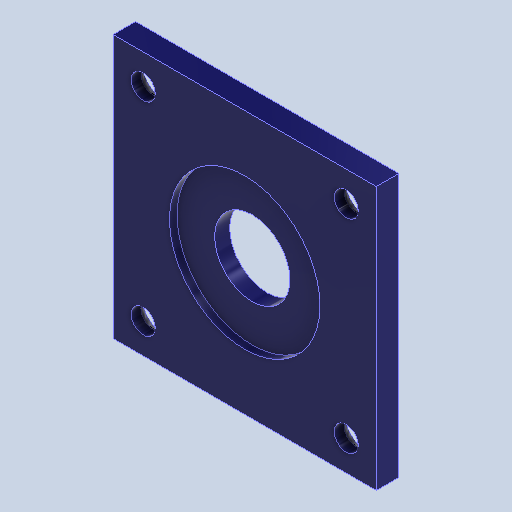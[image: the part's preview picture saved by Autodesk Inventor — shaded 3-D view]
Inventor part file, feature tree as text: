
AUTODESK INVENTOR PART (.ipt)
format: ipt  version: 2022 (Build 260153000, 153)  size: 152,064 bytes
history: native  units: mm
features: sketch x2, extrude x2, hole x1
ambient origin geometry x8: Origin, YZ Plane, XZ Plane, XY Plane, X Axis, Y Axis, Z Axis, Center Point
bodies: Solid1 (feature_tree)
feature tree (5):
  sketch  "Sketch1"  dims[d0=35.0mm d1=35.0mm]
  extrude  "Extrusion1"  Depth=35.0mm
  extrude  "Extrusion2"  Depth=2.0mm TaperAngle=360.0deg
  hole  "Hole2"  [1 undecoded]
  sketch  "Sketch2"  dims[d3=3.0mm d4=40.0mm d6=360.0deg d8=10.0mm d9=20.0mm d10=3.0mm d11=0.0mm d12=1.0mm d13=0.0mm d21=3.2mm d22=6.0mm d23=6.6mm d24=2.0mm d25=90.0deg d26=8.0mm d27=20.594885mm]
note: 1 required parameter value undecoded (feature->parameter linkage not recoverable at this tier; creation-order binding heuristic only, values carry confidence <= 0.55)
